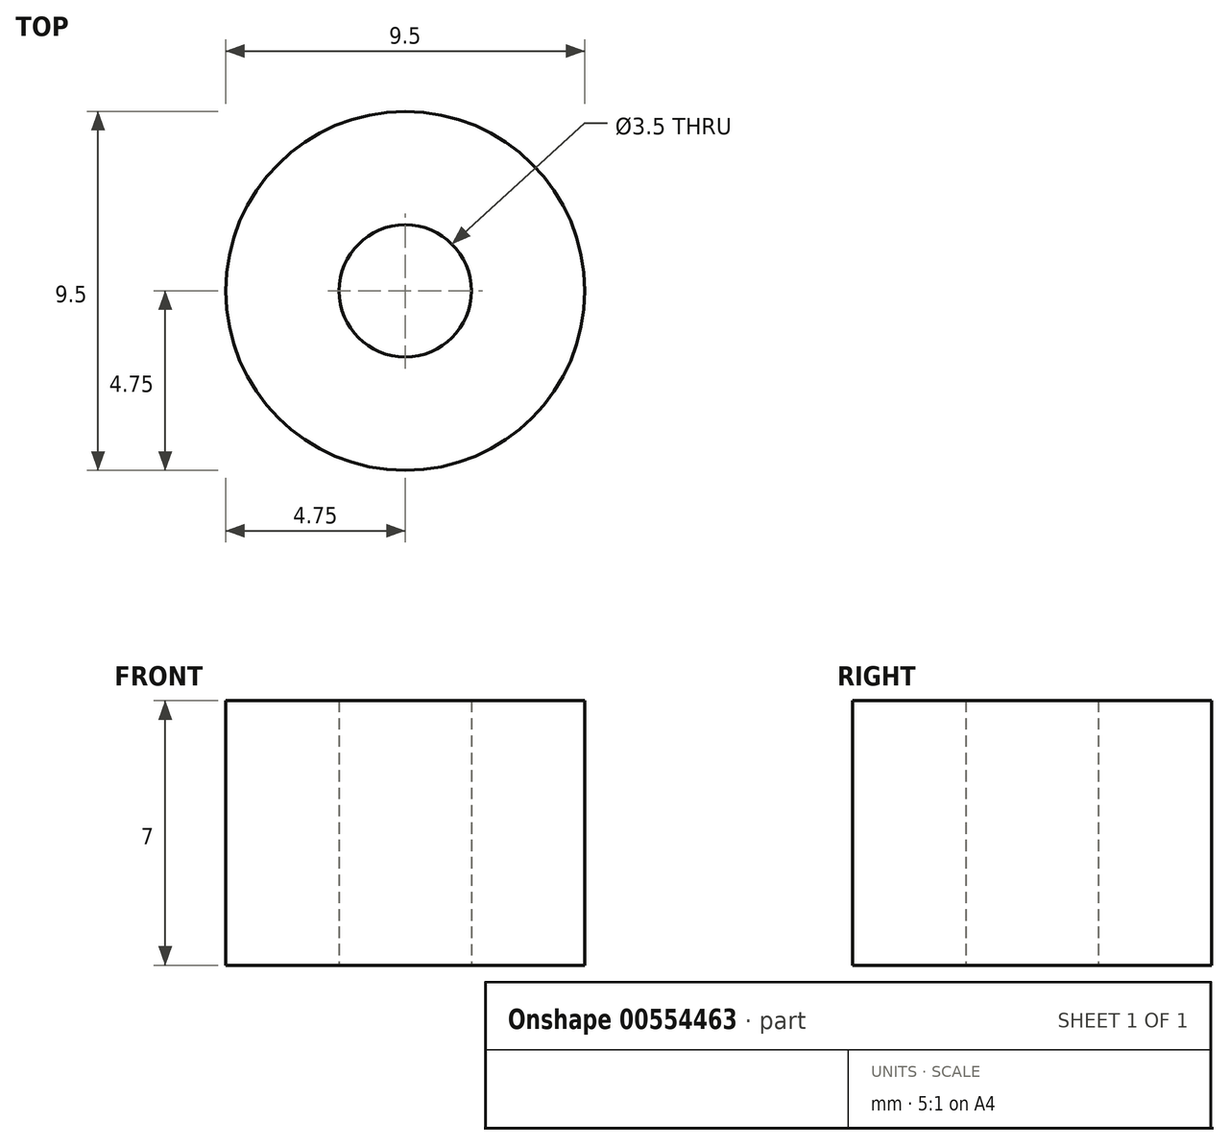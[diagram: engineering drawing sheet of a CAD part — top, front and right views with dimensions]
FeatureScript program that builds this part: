
annotation { "Feature Type Name" : "Feature", "Feature Type Description" : "" }
export const myFeature = defineFeature(function(context is Context, id is Id, definition is map)
    precondition{}
    {
        {
            var Q0;
            Q0=qCreatedBy(makeId("Top.planeOp"),FACE);
            var sketch = newSketch(context, id + "F0", { "sketchPlane" : qUnion([Q0])});
            skCircle(sketch, "E0", {"center": v(0, 0) * mm, "radius": 1.75 * mm});
            skCircle(sketch, "E1.0", {"center": v(0, 0) * mm, "radius": 4.75 * mm});
            skSolve(sketch);
        }
        {
            var Q0;
            Q0 = qSketchRegion(id + "F0", true);
            extrude(context, id + "F1", {"entities" : qUnion([Q0]), "depth" : 7 * mm, "offsetDistance" : 25 * mm});
        }
    });
